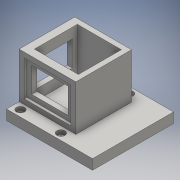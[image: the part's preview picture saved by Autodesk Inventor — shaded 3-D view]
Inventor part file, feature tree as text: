
AUTODESK INVENTOR PART (.ipt)
format: ipt  version: 2016 (Build 200138000, 138)  size: 186,880 bytes
history: native  units: mm
features: sketch x7, extrude x6, hole x1
ambient origin geometry x8: Origin, YZ Plane, XZ Plane, XY Plane, X Axis, Y Axis, Z Axis, Center Point
bodies: Solid1 (feature_tree)
feature tree (14):
  extrude  "Extrusion1"  Depth=42.5mm
  hole  "Hole1"  [1 undecoded]
  extrude  "Extrusion2"  Depth=40.0mm
  extrude  "Extrusion3"  Depth=67.5mm
  extrude  "Extrusion4"  Depth=56.0mm
  extrude  "Extrusion5"  Depth=2.5mm
  extrude  "Extrusion6"  Depth=5.0mm
  sketch  "Sketch1"  dims[d0=85.0mm d1=42.5mm]
  sketch  "Sketch2"  dims[d2=80.0mm d3=40.0mm]
  sketch  "Sketch3"  dims[d4=10.0mm d5=0.0mm d6=40.0mm]
  sketch  "Sketch4"  dims[d7=67.5mm d8=33.75mm]
  sketch  "Sketch5"  dims[d9=7.5mm]
  sketch  "Sketch6"  dims[d10=4.5mm d11=6.0mm d12=8.0mm d13=4.0mm d14=14.3117mm d15=8.0mm d16=20.594885mm d17=56.0mm]
  sketch  "Sketch7"  dims[d18=55.0mm d19=27.5mm d20=5.0mm d21=5.0mm d22=7.5mm d23=7.5mm d24=45.0mm d25=0.0mm d27=5.0mm d28=5.0mm d29=5.0mm d30=5.0mm d31=2.5mm d32=0.0mm d33=5.0mm d34=5.0mm d35=5.0mm d36=5.0mm d37=45.0mm d38=0.0mm d39=5.0mm d40=5.0mm d41=5.0mm d42=5.0mm d43=2.5mm d44=0.0mm d45=5.0mm d46=5.0mm d47=5.0mm d48=5.0mm d49=2.5mm d50=0.0mm]
note: 1 required parameter value undecoded (feature->parameter linkage not recoverable at this tier; creation-order binding heuristic only, values carry confidence <= 0.55)
